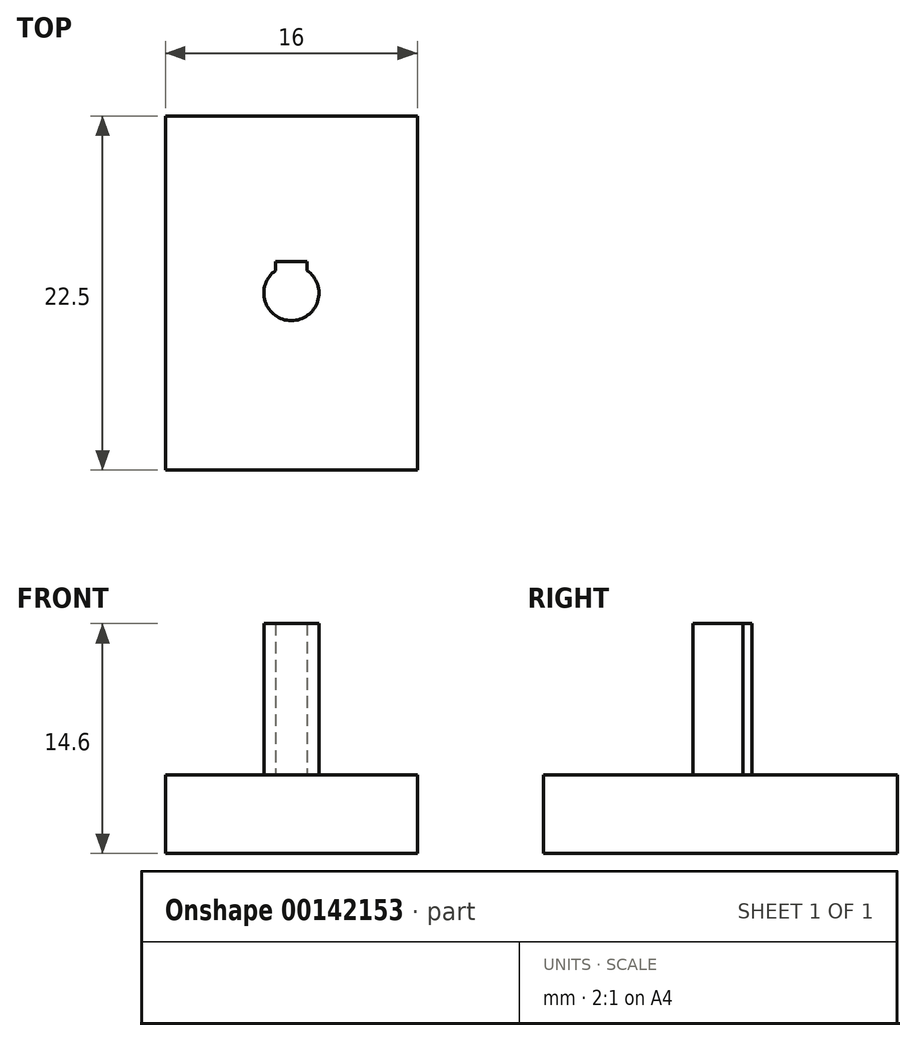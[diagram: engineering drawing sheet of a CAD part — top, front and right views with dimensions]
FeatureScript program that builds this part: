
annotation { "Feature Type Name" : "Feature", "Feature Type Description" : "" }
export const myFeature = defineFeature(function(context is Context, id is Id, definition is map)
    precondition{}
    {
        {
            var Q0;
            Q0=qCreatedBy(makeId("Front.planeOp"),FACE);
            var sketch = newSketch(context, id + "F0", { "sketchPlane" : qUnion([Q0])});
            skLineSegment(sketch, "E0", {"start": v(-8, 15.3) * mm, "end": v(8, 15.3) * mm});
            skLineSegment(sketch, "E1", {"start": v(-8, 10.3) * mm, "end": v(-8, 15.3) * mm});
            skLineSegment(sketch, "E2", {"start": v(-8, 10.3) * mm, "end": v(8, 10.3) * mm});
            skLineSegment(sketch, "E3", {"start": v(8, 10.3) * mm, "end": v(8, 15.3) * mm});
            skSolve(sketch);
        }
        {
            var Q0;
            Q0=makeQuery(id+"F0.imprint","IMPRINT",FACE,{"disambiguationData":[TD([[makeQuery(id+"F0.imprint","IMPRINT",EDGE,{"derivedFrom":sQuery(id+"F0.wireOp",EDGE,"E0")}),-1.0]])]});
            extrude(context, id + "F1", {"entities" : qUnion([Q0]), "depth" : 22.5 * mm});
        }
        {
            var Q0;
            Q0=makeQuery(id+"F1.opExtrude","SWEPT_FACE",FACE,{"disambiguationData":[OSD([sQuery(id+"F0.wireOp",EDGE,"E0")])]});
            var sketch = newSketch(context, id + "F2", { "sketchPlane" : qUnion([Q0])});
            skPoint(sketch, "E4.centerSnap0", {"position": v(-8, -11.25) * mm});
            skPoint(sketch, "E4.centerSnap1", {"position": v(0, 0) * mm});
            skArc(sketch, "E5", {"start": v(-1, -9.81) * mm, "mid": v(0, -13) * mm, "end": v(1, -9.81) * mm});
            skLineSegment(sketch, "E6.top", {"start": v(-1, -9.25) * mm, "end": v(1, -9.25) * mm});
            skLineSegment(sketch, "E6.left", {"start": v(-1, -9.81) * mm, "end": v(-1, -9.25) * mm});
            skLineSegment(sketch, "E6.right", {"start": v(1, -9.81) * mm, "end": v(1, -9.25) * mm});
            skPoint(sketch, "E6.bottom.start.orphan", {"position": v(-1, -11.25) * mm});
            skSolve(sketch);
        }
        {
            var Q0;
            Q0 = qSketchRegion(id + "F2", true);
            extrude(context, id + "F3", {"entities" : qUnion([Q0]), "operationType" : NewBodyOperationType.ADD, "depth" : 9.6 * mm});
        }
    });
